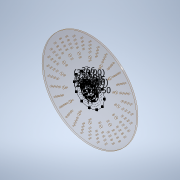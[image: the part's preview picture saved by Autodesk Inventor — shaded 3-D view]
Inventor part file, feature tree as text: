
AUTODESK INVENTOR PART (.ipt)
format: ipt  version: 2020 (Build 240168000, 168)  size: 514,560 bytes
history: native  units: in
note: dims shown in document units (in); Inventor stores cm internally (conversion verified against a paired STEP export)
features: sketch x4, extrude x3
ambient origin geometry x8: Origin, YZ Plane, XZ Plane, XY Plane, X Axis, Y Axis, Z Axis, Center Point
bodies: Solid1 (feature_tree)
feature tree (7):
  extrude  "Extrusion1"  Depth=0.25in
  extrude  "Extrusion2"  Depth=0.3937in
  extrude  "Extrusion3"  Depth=1.0in TaperAngle=0.0deg
  sketch  "Sketch3"  dims[d11=12.5984in d13=360.0deg d15=1.0in d16=0.0in]
  sketch  "Sketch1"  dims[d0=0.25in d1=0.0in d2=0.2031in]
  sketch  "Sketch2"  dims[d3=5.5in d4=1.5748in d6=0.5in d7=0.3937in d9=1.0in]
  sketch  "Sketch4"  dims[d17=2.497in d18=2.0in d19=3.625in d20=0.2656in d21=4.125in d22=2.5in d23=4.7244in d25=360.0deg d27=1.0in d28=0.0in d29=0.5079in d30=0.2031in d31=0.9375in d32=4.7244in d34=360.0deg d36=0.15in d37=45.0deg d38=1.35in d39=2.3622in d41=360.0deg]
